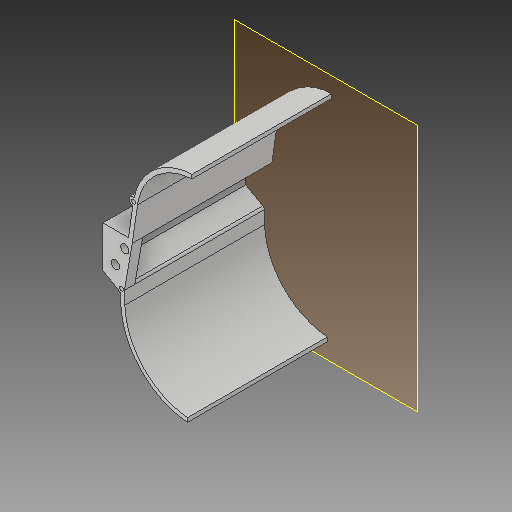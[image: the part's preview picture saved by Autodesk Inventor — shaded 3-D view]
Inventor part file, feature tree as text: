
AUTODESK INVENTOR PART (.ipt)
format: ipt  version: 2017 (Build 210142000, 142)  size: 169,984 bytes
history: native  units: mm
features: other x6, reference x4, plane x2, extrude x2, sketch x2, projected_geometry x1
ambient origin geometry x8: Origin, YZ Plane, XZ Plane, XY Plane, X Axis, Y Axis, Z Axis, Center Point
bodies: Solid1 (feature_tree)
feature tree (17):
  plane  "Work Plane1"
  extrude  "Extrusion1"  Depth=3.0mm
  sketch  "Sketch2"  dims[d2=3.0mm d3=125.0mm d4=0.0mm d5=125.0mm d6=0.0mm]
  plane  "Work Plane2"
  extrude  "Extrusion2"  Depth=125.0mm TaperAngle=0.0deg
  sketch  "Sketch1"  dims[d0=1.0mm d1=3.0mm]
  reference  "Reference1"
  reference  "Reference2"
  projected_geometry  "Projected Loop1"
  reference  "Reference3"
  reference  "Reference4"
  parser-record x1  (decoder bookkeeping rows leaked as tree rows — omitted from the tree; the rows remain in map.json)
  other  "gearbox.iam"
  other  "case part 1:1"
  other  "case bottom half:1"
  other  "fork:1"
  other  "fork:2"
note: 1 file-system path scrubbed to <path> (originals preserved in map.json)
